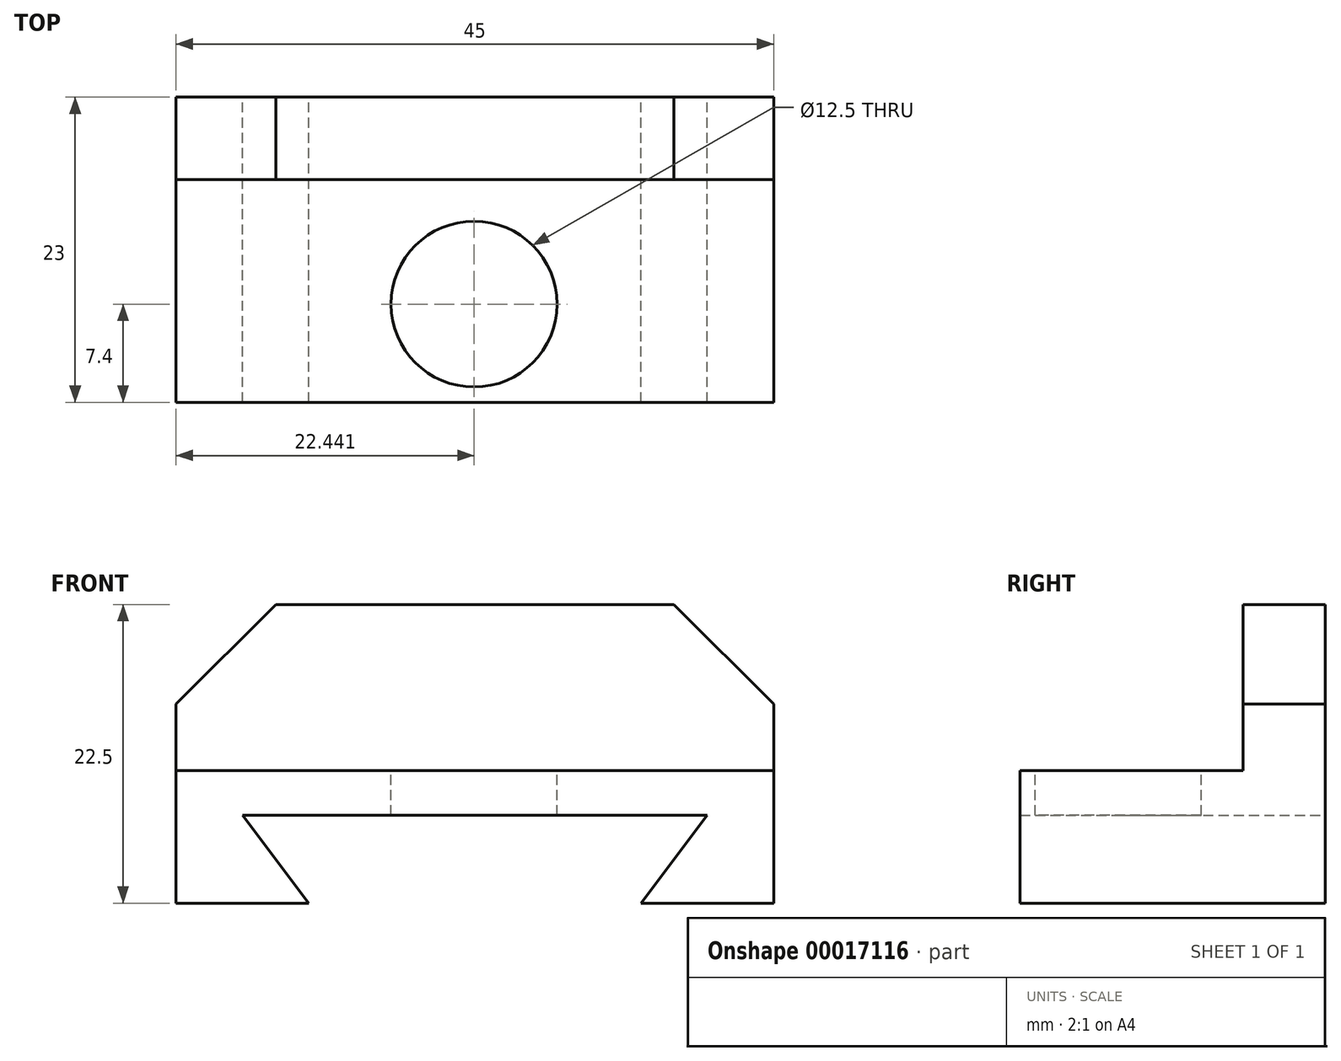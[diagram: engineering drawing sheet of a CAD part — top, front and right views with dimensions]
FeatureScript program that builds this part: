
annotation { "Feature Type Name" : "Feature", "Feature Type Description" : "" }
export const myFeature = defineFeature(function(context is Context, id is Id, definition is map)
    precondition{}
    {
        {
            var Q0;
            Q0=qCreatedBy(makeId("Front.planeOp"),FACE);
            var sketch = newSketch(context, id + "F0", { "sketchPlane" : qUnion([Q0])});
            skLineSegment(sketch, "E0", {"start": v(1.27, -18.7) * mm, "end": v(-8.73, -18.7) * mm});
            skLineSegment(sketch, "E1", {"start": v(-8.73, -18.7) * mm, "end": v(-8.73, -8.7) * mm});
            skLineSegment(sketch, "E2", {"start": v(-8.73, -8.7) * mm, "end": v(36.27, -8.7) * mm});
            skLineSegment(sketch, "E3", {"start": v(36.27, -8.7) * mm, "end": v(36.27, -18.7) * mm});
            skLineSegment(sketch, "E4", {"start": v(36.27, -18.7) * mm, "end": v(26.27, -18.7) * mm});
            skLineSegment(sketch, "E5", {"start": v(-8.73, -8.7) * mm, "end": v(-8.73, -3.7) * mm});
            skLineSegment(sketch, "E6", {"start": v(-8.73, -3.7) * mm, "end": v(-1.23, 3.8) * mm});
            skLineSegment(sketch, "E7", {"start": v(-1.23, 3.8) * mm, "end": v(28.77, 3.8) * mm});
            skLineSegment(sketch, "E8", {"start": v(28.77, 3.8) * mm, "end": v(36.27, -3.7) * mm});
            skLineSegment(sketch, "E9", {"start": v(36.27, -3.7) * mm, "end": v(36.27, -8.7) * mm});
            skLineSegment(sketch, "E10", {"start": v(1.27, -18.7) * mm, "end": v(-3.73, -12.07) * mm});
            skLineSegment(sketch, "E11", {"start": v(-3.73, -12.07) * mm, "end": v(31.27, -12.07) * mm});
            skLineSegment(sketch, "E12", {"start": v(31.27, -12.07) * mm, "end": v(26.27, -18.7) * mm});
            skSolve(sketch);
        }
        {
            var Q0;
            Q0=makeQuery(id+"F0.imprint","IMPRINT",FACE,{"disambiguationData":[TD([[makeQuery(id+"F0.imprint","IMPRINT",EDGE,{"derivedFrom":sQuery(id+"F0.wireOp",EDGE,"E0")}),-1.0]])]});
            extrude(context, id + "F1", {"entities" : qUnion([Q0]), "depth" : 23 * mm});
        }
        {
            var Q0;
            Q0=makeQuery(id+"F0.imprint","IMPRINT",FACE,{"disambiguationData":[TD([[makeQuery(id+"F0.imprint","IMPRINT",EDGE,{"derivedFrom":sQuery(id+"F0.wireOp",EDGE,"E2")}),1.0]])]});
            extrude(context, id + "F2", {"entities" : qUnion([Q0]), "operationType" : NewBodyOperationType.ADD, "depth" : 6.2 * mm});
        }
        {
            var Q0;
            Q0=makeQuery(id+"F1.opExtrude","SWEPT_FACE",FACE,{"disambiguationData":[OSD([sQuery(id+"F0.wireOp",EDGE,"E2")])]});
            var sketch = newSketch(context, id + "F3", { "sketchPlane" : qUnion([Q0])});
            skCircle(sketch, "E13", {"center": v(13.71, -15.6) * mm, "radius": 6.25 * mm});
            skSolve(sketch);
        }
        {
            var Q0;
            Q0=makeQuery(id+"F3.imprint","IMPRINT",FACE,{"disambiguationData":[TD([[makeQuery(id+"F3.imprint","IMPRINT",EDGE,{"derivedFrom":sQuery(id+"F3.wireOp",EDGE,"E13")}),1.0]])]});
            extrude(context, id + "F4", {"entities" : qUnion([Q0]), "operationType" : NewBodyOperationType.REMOVE, "endBound" : BoundingType.THROUGH_ALL, "oppositeDirection" : true, "depth" : 25 * mm});
        }
    });
